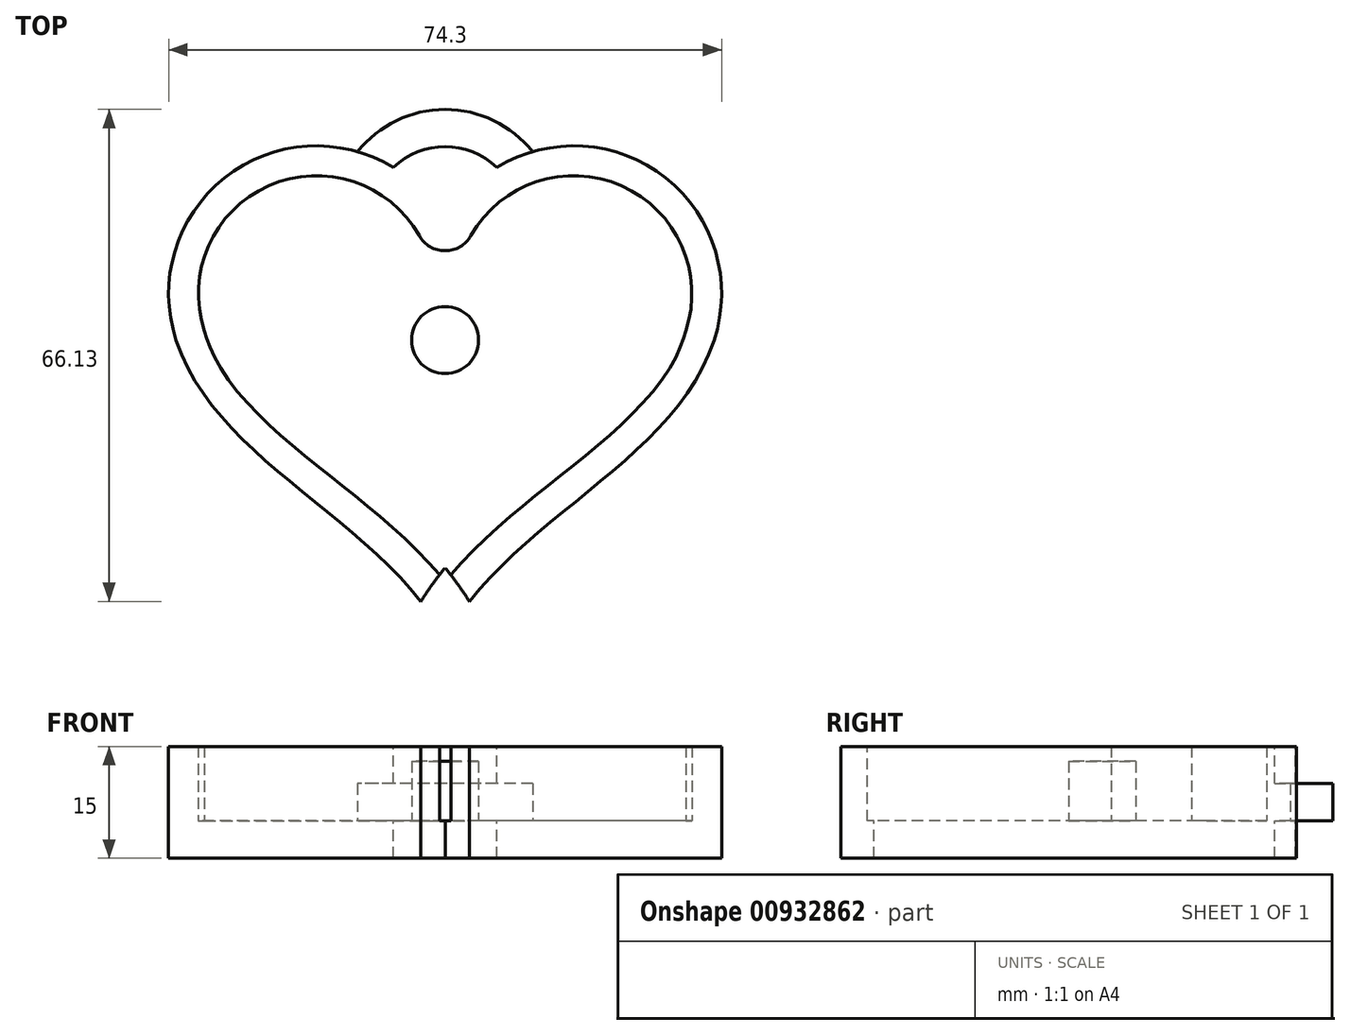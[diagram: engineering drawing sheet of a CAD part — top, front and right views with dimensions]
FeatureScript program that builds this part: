
annotation { "Feature Type Name" : "Feature", "Feature Type Description" : "" }
export const myFeature = defineFeature(function(context is Context, id is Id, definition is map)
    precondition{}
    {
        {
            var Q0;
            Q0=qCreatedBy(makeId("Top.planeOp"),FACE);
            var sketch = newSketch(context, id + "F0", { "sketchPlane" : qUnion([Q0])});
            skArc(sketch, "E0", {"start": v(0, 16) * mm, "mid": v(-25.33, 24.4) * mm, "end": v(-36.15, 0) * mm});
            skArc(sketch, "E1.MirrorC", {"start": v(0, 16) * mm, "mid": v(25.33, 24.4) * mm, "end": v(36.15, 0) * mm});
            skLineSegment(sketch, "E2", {"start": v(0, 10.83) * mm, "end": v(0, -30.91) * mm});
            skFitSpline(sketch, "E3", {"points": [v(-36.15, 0) * mm, v(0, -39.86) * mm], "startDerivative": vector(16.6, -49.96) * mm, "endDerivative": vector(28.05, -48.5) * mm});
            skFitSpline(sketch, "E4.MirrorCS", {"points": [v(36.15, 0) * mm, v(0, -39.86) * mm], "startDerivative": vector(-16.6, -49.96) * mm, "endDerivative": vector(-28.05, -48.5) * mm});
            skFitSpline(sketch, "E5.0.left", {"points": [v(-31.23, 1.63) * mm, v(-30.68, -0.03) * mm, v(-29.18, -3.14) * mm, v(-25.79, -7.55) * mm, v(-21.4, -11.82) * mm, v(-16.3, -16.08) * mm, v(-10.79, -20.5) * mm, v(-5.22, -25.28) * mm, v(0.07, -30.7) * mm, v(3.14, -34.95) * mm, v(4.48, -37.27) * mm]});
            skFitSpline(sketch, "E5.1.right", {"points": [v(31.23, 1.63) * mm, v(30.68, -0.03) * mm, v(29.18, -3.14) * mm, v(25.79, -7.55) * mm, v(21.4, -11.82) * mm, v(16.3, -16.08) * mm, v(10.79, -20.5) * mm, v(5.22, -25.28) * mm, v(-0.07, -30.7) * mm, v(-3.14, -34.95) * mm, v(-4.48, -37.27) * mm]});
            skArc(sketch, "E5.2.right", {"start": v(4.48, 13.41) * mm, "mid": v(23.21, 19.68) * mm, "end": v(31.23, 1.63) * mm});
            skArc(sketch, "E5.3.startCap", {"start": v(4.48, 13.41) * mm, "mid": v(-0.03, 10.83) * mm, "end": v(-4.51, 13.46) * mm});
            skArc(sketch, "E5.3.left", {"start": v(-4.51, 13.46) * mm, "mid": v(-23.29, 19.64) * mm, "end": v(-31.2, 1.52) * mm});
            skCircle(sketch, "E6", {"center": v(0, 0) * mm, "radius": 4.5 * mm});
            skArc(sketch, "E7", {"start": v(6.95, 23.2) * mm, "mid": v(0, 26) * mm, "end": v(-6.95, 23.2) * mm});
            skArc(sketch, "E8.trimOffspring", {"start": v(11.76, 25.32) * mm, "mid": v(0, 31) * mm, "end": v(-11.76, 25.32) * mm});
            skSolve(sketch);
        }
        {
            var Q0;
            {var subQ0=sQuery(id+"F0.wireOp",EDGE,"E5.1.right");Q0=makeQuery(id+"F0.imprint","IMPRINT",FACE,{"disambiguationData":[TD([[makeQuery(id+"F0.imprint","IMPRINT",EDGE,{"derivedFrom":subQ0}),-1.0]])]});}
            var Q1;
            {var subQ4=sQuery(id+"F0.wireOp",EDGE,"E0");Q1=makeQuery(id+"F0.imprint","IMPRINT",FACE,{"disambiguationData":[TD([[makeQuery(id+"F0.imprint","IMPRINT",EDGE,{"derivedFrom":subQ4}),1.0]])]});}
            var Q2;
            {var subQ0=sQuery(id+"F0.wireOp",EDGE,"E6");var subQ1=sQuery(id+"F0.wireOp",EDGE,"E2");var subQ2=makeQuery(id+"F0.imprint","INTERSECT",VERTEX,{"disambiguationData":[OD(0.0)],"derivedFrom":[subQ1,subQ0]});Q2=makeQuery(id+"F0.imprint","IMPRINT",FACE,{"disambiguationData":[TD([[makeQuery(id+"F0.imprint","IMPRINT",EDGE,{"disambiguationData":[TD([[subQ2,-1.0]])],"derivedFrom":subQ1}),1.0]])]});}
            var Q3;
            {var subQ0=sQuery(id+"F0.wireOp",EDGE,"E6");var subQ1=sQuery(id+"F0.wireOp",EDGE,"E2");var subQ2=makeQuery(id+"F0.imprint","INTERSECT",VERTEX,{"disambiguationData":[OD(0.0)],"derivedFrom":[subQ1,subQ0]});Q3=makeQuery(id+"F0.imprint","IMPRINT",FACE,{"disambiguationData":[TD([[makeQuery(id+"F0.imprint","IMPRINT",EDGE,{"disambiguationData":[TD([[subQ2,-1.0]])],"derivedFrom":subQ1}),-1.0]])]});}
            var Q4;
            {var subQ2=sQuery(id+"F0.wireOp",EDGE,"E1.MirrorC");Q4=makeQuery(id+"F0.imprint","IMPRINT",FACE,{"disambiguationData":[TD([[makeQuery(id+"F0.imprint","IMPRINT",EDGE,{"derivedFrom":subQ2}),-1.0]])]});}
            extrude(context, id + "F1", {"entities" : qUnion([Q0, Q1, Q2, Q3, Q4]), "depth" : -5 * mm, "offsetDistance" : 25 * mm});
        }
        {
            var Q0;
            {var subQ0=sQuery(id+"F0.wireOp",EDGE,"E6");var subQ1=sQuery(id+"F0.wireOp",EDGE,"E2");var subQ2=makeQuery(id+"F0.imprint","INTERSECT",VERTEX,{"disambiguationData":[OD(0.0)],"derivedFrom":[subQ1,subQ0]});Q0=makeQuery(id+"F0.imprint","IMPRINT",FACE,{"disambiguationData":[TD([[makeQuery(id+"F0.imprint","IMPRINT",EDGE,{"disambiguationData":[TD([[subQ2,-1.0]])],"derivedFrom":subQ1}),-1.0]])]});}
            var Q1;
            {var subQ0=sQuery(id+"F0.wireOp",EDGE,"E6");var subQ1=sQuery(id+"F0.wireOp",EDGE,"E2");var subQ2=makeQuery(id+"F0.imprint","INTERSECT",VERTEX,{"disambiguationData":[OD(0.0)],"derivedFrom":[subQ1,subQ0]});Q1=makeQuery(id+"F0.imprint","IMPRINT",FACE,{"disambiguationData":[TD([[makeQuery(id+"F0.imprint","IMPRINT",EDGE,{"disambiguationData":[TD([[subQ2,-1.0]])],"derivedFrom":subQ1}),1.0]])]});}
            extrude(context, id + "F2", {"entities" : qUnion([Q0, Q1]), "operationType" : NewBodyOperationType.ADD, "depth" : 8 * mm, "offsetDistance" : 25 * mm});
        }
        {
            var Q0;
            Q0=makeQuery(id+"F1.opExtrude","CAP_FACE",FACE,{"disambiguationData":[OSD([sQuery(id+"F0.wireOp",EDGE,"E0"),sQuery(id+"F0.wireOp",EDGE,"E1.MirrorC"),sQuery(id+"F0.wireOp",EDGE,"E3"),sQuery(id+"F0.wireOp",EDGE,"E4.MirrorCS")])],"isStart":true});
            var sketch = newSketch(context, id + "F3", { "sketchPlane" : qUnion([Q0])});
            skArc(sketch, "E9.JHR.JHR", {"start": v(0, 16) * mm, "mid": v(-25.33, 24.4) * mm, "end": v(-36.15, 0) * mm, "construction": true});
            skFitSpline(sketch, "E9.JHh.JHh", {"points": [v(-36.15, 0) * mm, v(-30.61, -16.65) * mm, v(-9.35, -23.7) * mm, v(0, -39.86) * mm], "construction": true});
            skFitSpline(sketch, "E9.JHp.JHp", {"points": [v(36.15, 0) * mm, v(30.61, -16.65) * mm, v(9.35, -23.7) * mm, v(0, -39.86) * mm], "construction": true});
            skArc(sketch, "E9.JHZ.JHZ", {"start": v(0, 16) * mm, "mid": v(25.33, 24.4) * mm, "end": v(36.15, 0) * mm, "construction": true});
            skArc(sketch, "E9.0.startCap", {"start": v(3.48, 14.04) * mm, "mid": v(0, 12) * mm, "end": v(-3.48, 14.04) * mm});
            skArc(sketch, "E9.0.endCap", {"start": v(-39.94, -1.26) * mm, "mid": v(-39.94, -1.26) * mm, "end": v(-39.94, -1.26) * mm});
            skArc(sketch, "E9.0.left", {"start": v(-3.48, 14.04) * mm, "mid": v(-23.71, 20.74) * mm, "end": v(-32.35, 1.26) * mm});
            skArc(sketch, "E9.1.startCap", {"start": v(-39.94, -1.26) * mm, "mid": v(-39.94, -1.26) * mm, "end": v(-39.94, -1.26) * mm});
            skFitSpline(sketch, "E9.1.left", {"points": [v(-32.35, 1.26) * mm, v(-31.77, -0.5) * mm, v(-30.18, -3.78) * mm, v(-26.66, -8.35) * mm, v(-22.18, -12.7) * mm, v(-17.03, -17) * mm, v(-11.53, -21.4) * mm, v(-6.02, -26.14) * mm, v(-0.83, -31.48) * mm, v(2.16, -35.6) * mm, v(3.46, -37.86) * mm]});
            skArc(sketch, "E9.2.startCap", {"start": v(39.94, -1.26) * mm, "mid": v(39.94, -1.26) * mm, "end": v(39.94, -1.26) * mm});
            skFitSpline(sketch, "E9.2.right", {"points": [v(32.35, 1.26) * mm, v(31.77, -0.5) * mm, v(30.18, -3.78) * mm, v(26.66, -8.35) * mm, v(22.18, -12.7) * mm, v(17.03, -17) * mm, v(11.53, -21.4) * mm, v(6.02, -26.14) * mm, v(0.83, -31.48) * mm, v(-2.16, -35.6) * mm, v(-3.46, -37.86) * mm]});
            skArc(sketch, "E9.3.startCap", {"start": v(3.48, 14.04) * mm, "mid": v(0, 12) * mm, "end": v(-3.48, 14.04) * mm});
            skArc(sketch, "E9.3.endCap", {"start": v(39.94, -1.26) * mm, "mid": v(39.94, -1.26) * mm, "end": v(39.94, -1.26) * mm});
            skArc(sketch, "E9.3.right", {"start": v(3.48, 14.04) * mm, "mid": v(23.71, 20.74) * mm, "end": v(32.35, 1.26) * mm});
            skSolve(sketch);
        }
        {
            var Q0;
            {var subQ4=sQuery(id+"F3.wireOp",EDGE,"E9.0.left");Q0=makeQuery(id+"F3.imprint","IMPRINT",FACE,{"disambiguationData":[TD([[makeQuery(id+"F3.imprint","IMPRINT",EDGE,{"derivedFrom":subQ4}),-1.0]])]});}
            extrude(context, id + "F4", {"entities" : qUnion([Q0]), "operationType" : NewBodyOperationType.ADD, "depth" : 10 * mm, "offsetDistance" : 25 * mm});
        }
        {
            var Q0;
            {var subQ0=sQuery(id+"F0.wireOp",EDGE,"E7");Q0=makeQuery(id+"F0.imprint","IMPRINT",FACE,{"disambiguationData":[TD([[makeQuery(id+"F0.imprint","IMPRINT",EDGE,{"derivedFrom":subQ0}),-1.0]])]});}
            extrude(context, id + "F5", {"entities" : qUnion([Q0]), "operationType" : NewBodyOperationType.ADD, "depth" : 5 * mm, "offsetDistance" : 25 * mm});
        }
    });
